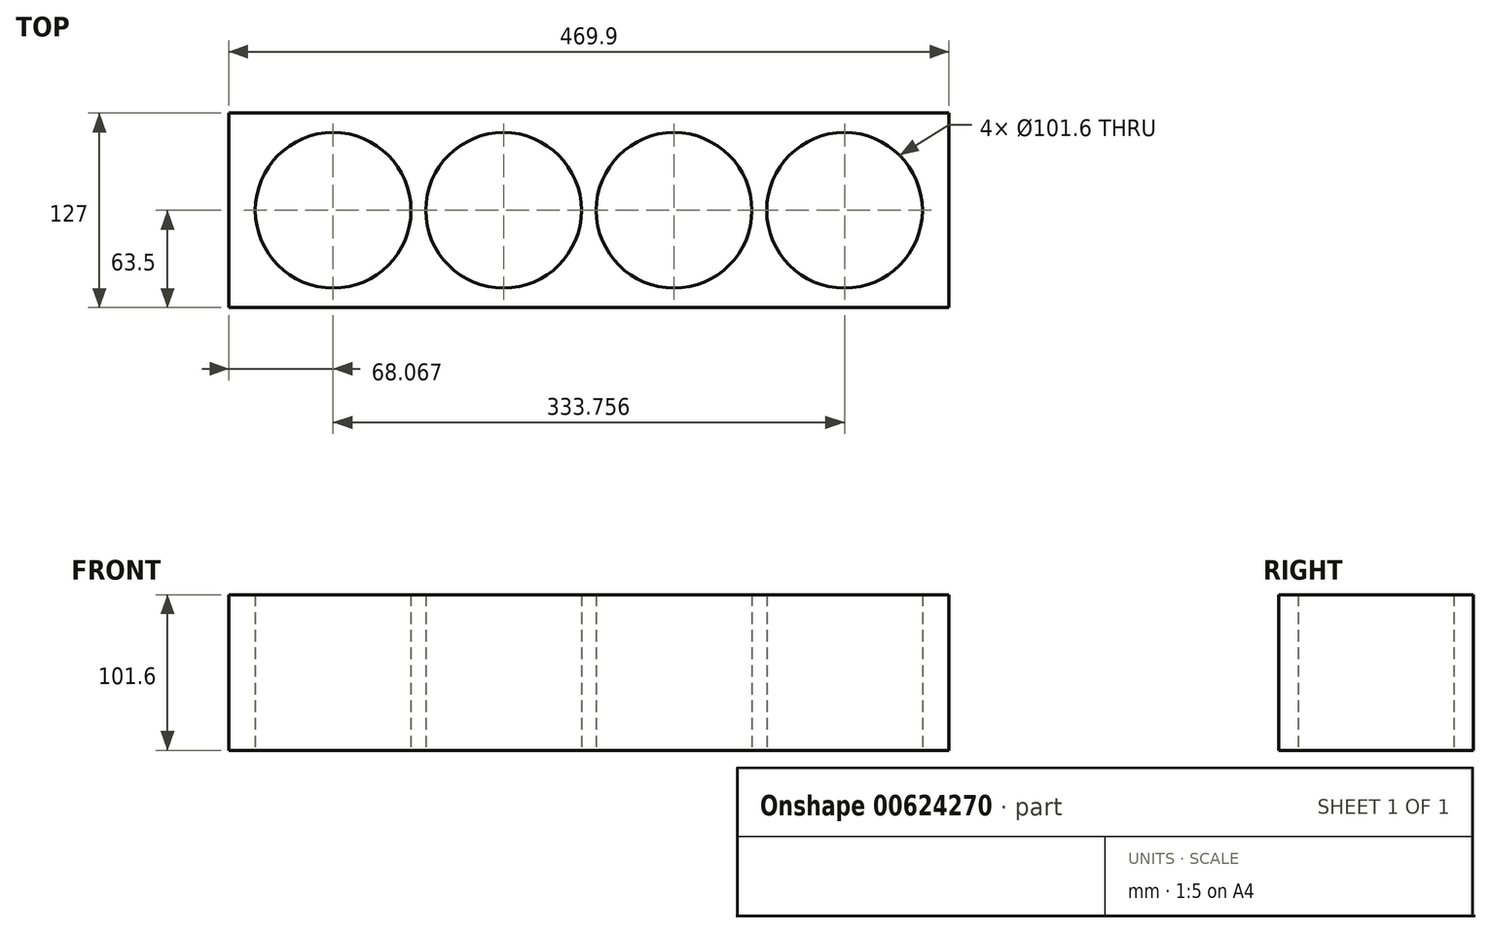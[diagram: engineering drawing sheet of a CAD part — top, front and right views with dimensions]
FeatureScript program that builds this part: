
annotation { "Feature Type Name" : "Feature", "Feature Type Description" : "" }
export const myFeature = defineFeature(function(context is Context, id is Id, definition is map)
    precondition{}
    {
        {
            var Q0;
            Q0=qCreatedBy(makeId("Top.planeOp"),FACE);
            var sketch = newSketch(context, id + "F0", { "sketchPlane" : qUnion([Q0])});
            skCircle(sketch, "E0", {"center": v(-165.8, 0) * mm, "radius": 50.8 * mm});
            skCircle(sketch, "E1.1.0.0", {"center": v(-54.55, 0) * mm, "radius": 50.8 * mm});
            skCircle(sketch, "E1.2.0.0", {"center": v(56.7, 0) * mm, "radius": 50.8 * mm});
            skCircle(sketch, "E1.3.0.0", {"center": v(167.95, 0) * mm, "radius": 50.8 * mm});
            skLineSegment(sketch, "E1.direction1", {"start": v(-165.8, 0) * mm, "end": v(-54.55, 0) * mm, "construction": true});
            skLineSegment(sketch, "E2", {"start": v(-165.8, 0) * mm, "end": v(167.95, 0) * mm, "construction": true});
            skLineSegment(sketch, "E3.bottom", {"start": v(236.03, 63.5) * mm, "end": v(-233.87, 63.5) * mm});
            skLineSegment(sketch, "E3.top", {"start": v(236.03, -63.5) * mm, "end": v(-233.87, -63.5) * mm});
            skLineSegment(sketch, "E3.left", {"start": v(236.03, 63.5) * mm, "end": v(236.03, -63.5) * mm});
            skLineSegment(sketch, "E3.right", {"start": v(-233.87, 63.5) * mm, "end": v(-233.87, -63.5) * mm});
            skPoint(sketch, "E3.middle", {"position": v(1.08, 0) * mm});
            skSolve(sketch);
        }
        {
            var Q0;
            Q0=makeQuery(id+"F0.imprint","IMPRINT",FACE,{"disambiguationData":[TD([[makeQuery(id+"F0.imprint","IMPRINT",EDGE,{"derivedFrom":sQuery(id+"F0.wireOp",EDGE,"E0")}),-1.0]])]});
            extrude(context, id + "F1", {"entities" : qUnion([Q0]), "depth" : 101.6 * mm, "offsetDistance" : 25.4 * mm});
        }
    });
